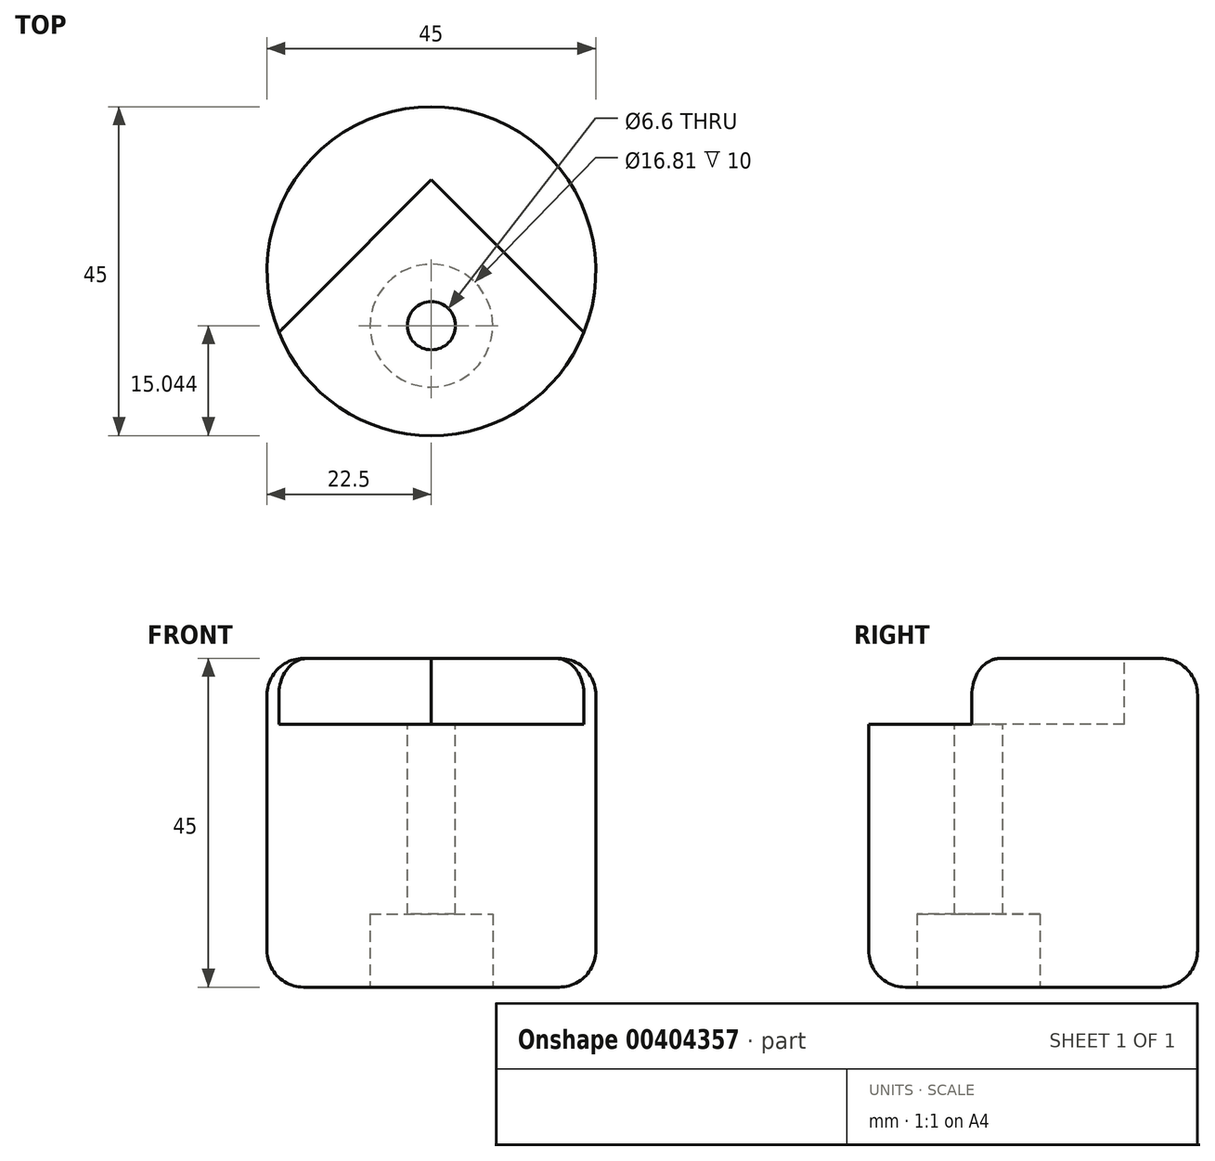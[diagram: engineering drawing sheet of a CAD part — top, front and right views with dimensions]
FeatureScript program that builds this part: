
annotation { "Feature Type Name" : "Feature", "Feature Type Description" : "" }
export const myFeature = defineFeature(function(context is Context, id is Id, definition is map)
    precondition{}
    {
        {
            var Q0;
            Q0=qCreatedBy(makeId("Top.planeOp"),FACE);
            var sketch = newSketch(context, id + "F0", { "sketchPlane" : qUnion([Q0])});
            skCircle(sketch, "E0", {"center": v(0, 0) * mm, "radius": 22.5 * mm});
            skSolve(sketch);
        }
        {
            var Q0;
            Q0 = qSketchRegion(id + "F0", true);
            extrude(context, id + "F1", {"entities" : qUnion([Q0]), "endBound" : BoundingType.SYMMETRIC, "depth" : 45 * mm});
        }
        {
            var Q0;
            Q0=makeQuery(id+"F1.opExtrude","CAP_FACE",FACE,{"disambiguationData":[OSD([sQuery(id+"F0.wireOp",EDGE,"E0")])],"isStart":false});
            var sketch = newSketch(context, id + "F2", { "sketchPlane" : qUnion([Q0])});
            skPoint(sketch, "E1", {"position": v(0, 12.5) * mm});
            skLineSegment(sketch, "E2", {"start": v(0, 12.5) * mm, "end": v(0, -22.5) * mm, "construction": true});
            skLineSegment(sketch, "E3", {"start": v(0, 12.5) * mm, "end": v(-20.88, -8.38) * mm});
            skLineSegment(sketch, "E4", {"start": v(0, 12.5) * mm, "end": v(20.88, -8.38) * mm});
            skSolve(sketch);
        }
        {
            var Q0;
            {var subQ0=sQuery(id+"F2.wireOp",EDGE,"E3");Q0=makeQuery(id+"F2.imprint","IMPRINT",FACE,{"disambiguationData":[TD([[makeQuery(id+"F2.imprint","IMPRINT",EDGE,{"derivedFrom":subQ0}),1.0]])]});}
            extrude(context, id + "F3", {"entities" : qUnion([Q0]), "operationType" : NewBodyOperationType.REMOVE, "oppositeDirection" : true, "depth" : 9 * mm});
        }
        {
            var Q0;
            Q0=makeQuery(id+"F1.opExtrude","CAP_EDGE",EDGE,{"disambiguationData":[OSD([sQuery(id+"F0.wireOp",EDGE,"E0")])],"isStart":true});
            fillet(context, id + "F4", {"entities" : qUnion([Q0]), "radius" : 5 * mm, "tangentPropagation" : true, "allowEdgeOverflow" : false});
        }
        {
            var Q0;
            Q0=makeQuery(id+"F1.opExtrude","CAP_EDGE",EDGE,{"disambiguationData":[OSD([sQuery(id+"F0.wireOp",EDGE,"E0")])],"isStart":false});
            fillet(context, id + "F5", {"entities" : qUnion([Q0]), "radius" : 5 * mm, "tangentPropagation" : true, "allowEdgeOverflow" : false});
        }
        {
            var Q0;
            Q0=makeQuery(id+"F3.boolean.opBoolean","COPY",FACE,{"derivedFrom":makeQuery(id+"F3.opExtrude","CAP_FACE",FACE,{"disambiguationData":[OSD([sQuery(id+"F0.wireOp",EDGE,"E0"),sQuery(id+"F2.wireOp",EDGE,"E3"),sQuery(id+"F2.wireOp",EDGE,"E4")])],"isStart":false})});
            var sketch = newSketch(context, id + "F6", { "sketchPlane" : qUnion([Q0])});
            skPoint(sketch, "E5.positionSnap0", {"position": v(0, -22.5) * mm});
            skPoint(sketch, "E6", {"position": v(0, -7.46) * mm});
            skCircle(sketch, "E7", {"center": v(0, -7.46) * mm, "radius": 3.25 * mm});
            skSolve(sketch);
        }
        {
            var Q0;
            Q0=sQuery(id+"F6.wireOp",VERTEX,"E6");
            var Q1;
            Q1=makeQuery(id+"F1.opExtrude","SWEPT_BODY",BODY,{"disambiguationData":[OSD([sQuery(id+"F0.wireOp",EDGE,"E0")])]});
            hole(context, id + "F7", {"style" : HoleStyle.SIMPLE, "endStyle" : HoleEndStyle.THROUGH, "standardTappedOrClearance" : lookupTablePath({ "standard" : "ISO", "fit" : "Normal", "size" : "M6", "type" : "Clearance" }), "standardBlindInLast" : lookupTablePath({ "fit" : "Standard", "standard" : "ISO", "size" : "M6", "type" : "Clearance" }), "holeDiameter" : 6.6 * mm, "isTappedThrough" : true, "tappedDepth" : 12 * mm, "tapClearance" : 3, "locations" : qUnion([Q0]), "scope" : qUnion([Q1])});
        }
        {
            var Q0;
            Q0=makeQuery(id+"F1.opExtrude","CAP_FACE",FACE,{"disambiguationData":[OSD([sQuery(id+"F0.wireOp",EDGE,"E0")])],"isStart":true});
            var sketch = newSketch(context, id + "F8", { "sketchPlane" : qUnion([Q0])});
            skCircle(sketch, "E8", {"center": v(0, 7.46) * mm, "radius": 8.4 * mm});
            skSolve(sketch);
        }
        {
            var Q0;
            Q0=makeQuery(id+"F8.imprint","IMPRINT",FACE,{"disambiguationData":[TD([[makeQuery(id+"F8.imprint","IMPRINT",EDGE,{"derivedFrom":sQuery(id+"F8.wireOp",EDGE,"E8")}),1.0]])]});
            var Q1;
            Q1=sQuery(id+"F8.wireOp",EDGE,"E8");
            extrude(context, id + "F9", {"entities" : qUnion([Q0]), "operationType" : NewBodyOperationType.REMOVE, "surfaceEntities" : qUnion([Q1]), "oppositeDirection" : true, "depth" : 10 * mm});
        }
    });
